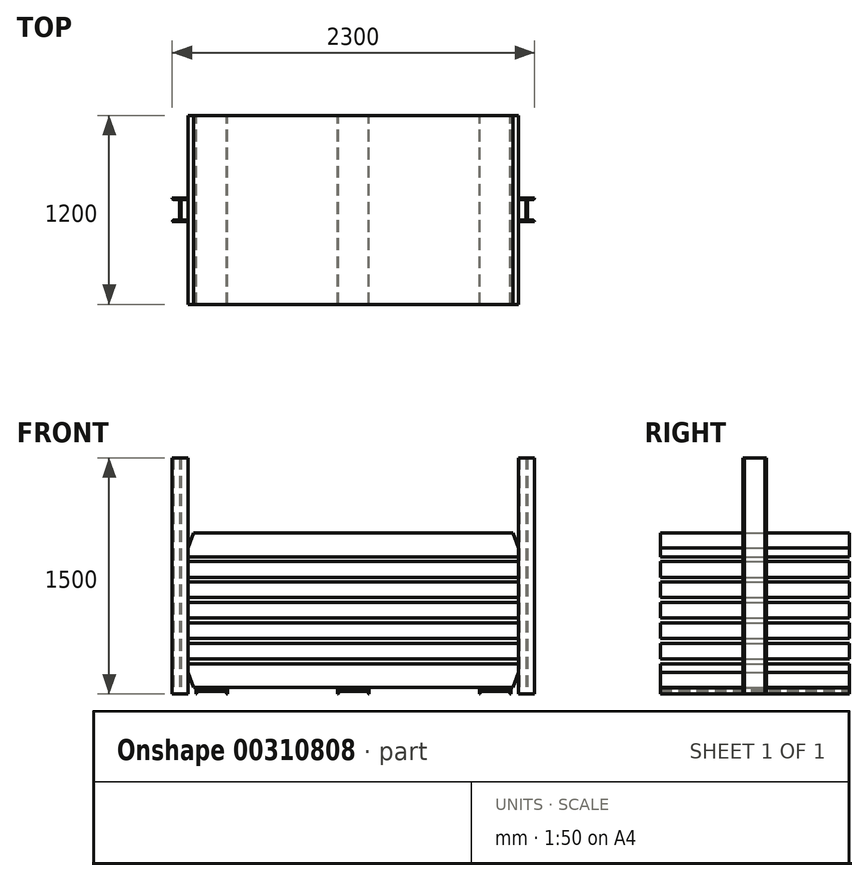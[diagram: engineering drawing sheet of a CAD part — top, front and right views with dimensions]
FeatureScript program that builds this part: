
annotation { "Feature Type Name" : "Feature", "Feature Type Description" : "" }
export const myFeature = defineFeature(function(context is Context, id is Id, definition is map)
    precondition{}
    {
        {
            var Q0;
            Q0=qCreatedBy(makeId("Front.planeOp"),FACE);
            var sketch = newSketch(context, id + "F0", { "sketchPlane" : qUnion([Q0])});
            skLineSegment(sketch, "E0", {"start": v(-100, 0) * mm, "end": v(100, 0) * mm, "construction": true});
            skLineSegment(sketch, "E1", {"start": v(0, -21.07) * mm, "end": v(0, 27.31) * mm, "construction": true});
            skPoint(sketch, "E1.startSnap0", {"position": v(0, 0) * mm});
            skLineSegment(sketch, "E2", {"start": v(-100, 20) * mm, "end": v(-100, -20) * mm});
            skLineSegment(sketch, "E3.0", {"start": v(-95, 15.24) * mm, "end": v(-95, 2.5) * mm});
            skLineSegment(sketch, "E4.0", {"start": v(-95, 2.5) * mm, "end": v(95, 2.5) * mm});
            skLineSegment(sketch, "E5.0", {"start": v(-95, -2.5) * mm, "end": v(95, -2.5) * mm});
            skLineSegment(sketch, "E6.trimOffspring", {"start": v(-95, -2.5) * mm, "end": v(-95, -15.24) * mm});
            skArc(sketch, "E7", {"start": v(-95, 15.24) * mm, "mid": v(-96.55, 18.62) * mm, "end": v(-100, 20) * mm});
            skArc(sketch, "E8.MirrorCS", {"start": v(-95, -15.24) * mm, "mid": v(-96.55, -18.62) * mm, "end": v(-100, -20) * mm});
            skLineSegment(sketch, "E9.MirrorCS", {"start": v(100, 20) * mm, "end": v(100, -20) * mm});
            skArc(sketch, "E10.MirrorCS", {"start": v(95, -15.24) * mm, "mid": v(96.55, -18.62) * mm, "end": v(100, -20) * mm});
            skLineSegment(sketch, "E11.MirrorCS", {"start": v(95, -2.5) * mm, "end": v(95, -15.24) * mm});
            skLineSegment(sketch, "E12.MirrorCS", {"start": v(95, 15.24) * mm, "end": v(95, 2.5) * mm});
            skArc(sketch, "E13.MirrorCS", {"start": v(95, 15.24) * mm, "mid": v(96.55, 18.62) * mm, "end": v(100, 20) * mm});
            skLineSegment(sketch, "E14.1.0.0", {"start": v(805, 2.5) * mm, "end": v(995, 2.5) * mm});
            skLineSegment(sketch, "E14.1.0.1", {"start": v(805, -2.5) * mm, "end": v(995, -2.5) * mm});
            skPoint(sketch, "E14.1.0.2", {"position": v(900, 0) * mm});
            skLineSegment(sketch, "E14.1.0.3", {"start": v(900, -21.07) * mm, "end": v(900, 27.31) * mm, "construction": true});
            skLineSegment(sketch, "E14.1.0.4", {"start": v(800, 0) * mm, "end": v(1000, 0) * mm, "construction": true});
            skLineSegment(sketch, "E14.1.0.5", {"start": v(1000, 20) * mm, "end": v(1000, -20) * mm});
            skArc(sketch, "E14.1.0.6", {"start": v(805, 15.24) * mm, "mid": v(803.45, 18.62) * mm, "end": v(800, 20) * mm});
            skLineSegment(sketch, "E14.1.0.7", {"start": v(995, -2.5) * mm, "end": v(995, -15.24) * mm});
            skLineSegment(sketch, "E14.1.0.8", {"start": v(800, 20) * mm, "end": v(800, -20) * mm});
            skLineSegment(sketch, "E14.1.0.9", {"start": v(995, 15.24) * mm, "end": v(995, 2.5) * mm});
            skLineSegment(sketch, "E14.1.0.10", {"start": v(805, 15.24) * mm, "end": v(805, 2.5) * mm});
            skLineSegment(sketch, "E14.1.0.11", {"start": v(805, -2.5) * mm, "end": v(805, -15.24) * mm});
            skArc(sketch, "E14.1.0.12", {"start": v(995, -15.24) * mm, "mid": v(996.55, -18.62) * mm, "end": v(1000, -20) * mm});
            skArc(sketch, "E14.1.0.13", {"start": v(805, -15.24) * mm, "mid": v(803.45, -18.62) * mm, "end": v(800, -20) * mm});
            skArc(sketch, "E14.1.0.14", {"start": v(995, 15.24) * mm, "mid": v(996.55, 18.62) * mm, "end": v(1000, 20) * mm});
            skLineSegment(sketch, "E14.direction1", {"start": v(-100, -20) * mm, "end": v(800, -20) * mm, "construction": true});
            skLineSegment(sketch, "E15.direction1", {"start": v(-100, -20) * mm, "end": v(-1000, -20) * mm, "construction": true});
            skPoint(sketch, "E16.orphan", {"position": v(-95, 15.24) * mm});
            skLineSegment(sketch, "E17.bottom", {"start": v(-1015, 22.23) * mm, "end": v(1015, 22.23) * mm});
            skLineSegment(sketch, "E17.top", {"start": v(-1050, 172.23) * mm, "end": v(1050, 172.23) * mm});
            skLineSegment(sketch, "E17.left", {"start": v(-1050, 117.23) * mm, "end": v(-1050, 172.23) * mm});
            skLineSegment(sketch, "E17.right", {"start": v(1050, 117.23) * mm, "end": v(1050, 172.23) * mm});
            skLineSegment(sketch, "E18", {"start": v(-1015, 22.23) * mm, "end": v(-1050, 117.23) * mm});
            skLineSegment(sketch, "E19.MirrorCS", {"start": v(1015, 22.23) * mm, "end": v(1050, 117.23) * mm});
            skLineSegment(sketch, "E20.bottom", {"start": v(-1050, 202.23) * mm, "end": v(1050, 202.23) * mm});
            skLineSegment(sketch, "E20.top", {"start": v(-1050, 302.23) * mm, "end": v(1050, 302.23) * mm});
            skLineSegment(sketch, "E20.left", {"start": v(-1050, 202.23) * mm, "end": v(-1050, 302.23) * mm});
            skLineSegment(sketch, "E20.right", {"start": v(1050, 202.23) * mm, "end": v(1050, 302.23) * mm});
            skLineSegment(sketch, "E21.0.1.0", {"start": v(-1050, 332.23) * mm, "end": v(1050, 332.23) * mm});
            skLineSegment(sketch, "E21.0.1.1", {"start": v(1050, 332.23) * mm, "end": v(1050, 432.23) * mm});
            skLineSegment(sketch, "E21.0.1.2", {"start": v(-1050, 332.23) * mm, "end": v(-1050, 432.23) * mm});
            skLineSegment(sketch, "E21.0.1.3", {"start": v(-1050, 432.23) * mm, "end": v(1050, 432.23) * mm});
            skLineSegment(sketch, "E21.0.2.0", {"start": v(-1050, 462.23) * mm, "end": v(1050, 462.23) * mm});
            skLineSegment(sketch, "E21.0.2.1", {"start": v(1050, 462.23) * mm, "end": v(1050, 562.23) * mm});
            skLineSegment(sketch, "E21.0.2.2", {"start": v(-1050, 462.23) * mm, "end": v(-1050, 562.23) * mm});
            skLineSegment(sketch, "E21.0.2.3", {"start": v(-1050, 562.23) * mm, "end": v(1050, 562.23) * mm});
            skLineSegment(sketch, "E21.0.3.0", {"start": v(-1050, 592.23) * mm, "end": v(1050, 592.23) * mm});
            skLineSegment(sketch, "E21.0.3.1", {"start": v(1050, 592.23) * mm, "end": v(1050, 692.23) * mm});
            skLineSegment(sketch, "E21.0.3.2", {"start": v(-1050, 592.23) * mm, "end": v(-1050, 692.23) * mm});
            skLineSegment(sketch, "E21.0.3.3", {"start": v(-1050, 692.23) * mm, "end": v(1050, 692.23) * mm});
            skLineSegment(sketch, "E21.direction1", {"start": v(-1050, 202.23) * mm, "end": v(-1025, 202.23) * mm, "construction": true});
            skLineSegment(sketch, "E21.direction2", {"start": v(-1050, 202.23) * mm, "end": v(-1050, 332.23) * mm, "construction": true});
            skLineSegment(sketch, "E22.0.1.0", {"start": v(-995, 2.5) * mm, "end": v(-805, 2.5) * mm});
            skLineSegment(sketch, "E22.3.1.0", {"start": v(-995, -2.5) * mm, "end": v(-805, -2.5) * mm});
            skPoint(sketch, "E22.6.1.0", {"position": v(-900, 0) * mm});
            skLineSegment(sketch, "E22.7.1.0", {"start": v(-1000, 0) * mm, "end": v(-800, 0) * mm, "construction": true});
            skLineSegment(sketch, "E22.10.1.0", {"start": v(-900, -21.07) * mm, "end": v(-900, 27.31) * mm, "construction": true});
            skArc(sketch, "E22.13.1.0", {"start": v(-805, -15.24) * mm, "mid": v(-803.45, -18.62) * mm, "end": v(-800, -20) * mm});
            skLineSegment(sketch, "E22.17.1.0", {"start": v(-805, -2.5) * mm, "end": v(-805, -15.24) * mm});
            skArc(sketch, "E22.20.1.0", {"start": v(-805, 15.24) * mm, "mid": v(-803.45, 18.62) * mm, "end": v(-800, 20) * mm});
            skLineSegment(sketch, "E22.24.1.0", {"start": v(-1000, 20) * mm, "end": v(-1000, -20) * mm});
            skLineSegment(sketch, "E22.27.1.0", {"start": v(-995, 15.24) * mm, "end": v(-995, 2.5) * mm});
            skPoint(sketch, "E22.28.1.0", {"position": v(-995, 15.24) * mm});
            skLineSegment(sketch, "E22.30.1.0", {"start": v(-995, -2.5) * mm, "end": v(-995, -15.24) * mm});
            skArc(sketch, "E22.33.1.0", {"start": v(-995, 15.24) * mm, "mid": v(-996.55, 18.62) * mm, "end": v(-1000, 20) * mm});
            skArc(sketch, "E22.37.1.0", {"start": v(-995, -15.24) * mm, "mid": v(-996.55, -18.62) * mm, "end": v(-1000, -20) * mm});
            skLineSegment(sketch, "E22.41.1.0", {"start": v(-800, 20) * mm, "end": v(-800, -20) * mm});
            skLineSegment(sketch, "E22.44.1.0", {"start": v(-805, 15.24) * mm, "end": v(-805, 2.5) * mm});
            skLineSegment(sketch, "E23.0.0.4", {"start": v(-1050, 722.23) * mm, "end": v(1050, 722.23) * mm});
            skLineSegment(sketch, "E23.3.0.4", {"start": v(1050, 722.23) * mm, "end": v(1050, 822.23) * mm});
            skLineSegment(sketch, "E23.6.0.4", {"start": v(-1050, 722.23) * mm, "end": v(-1050, 822.23) * mm});
            skLineSegment(sketch, "E23.9.0.4", {"start": v(-1050, 822.23) * mm, "end": v(1050, 822.23) * mm});
            skLineSegment(sketch, "E24", {"start": v(-1137.17, 512.23) * mm, "end": v(1108.9, 512.23) * mm, "construction": true});
            skPoint(sketch, "E24.startSnap0", {"position": v(-1050, 512.23) * mm});
            skPoint(sketch, "E24.endSnap0", {"position": v(1050, 512.23) * mm});
            skLineSegment(sketch, "E25.MirrorCS", {"start": v(-1050, 907.23) * mm, "end": v(-1050, 852.23) * mm});
            skLineSegment(sketch, "E26.MirrorCS", {"start": v(-1015, 1002.23) * mm, "end": v(-1050, 907.23) * mm});
            skLineSegment(sketch, "E27.MirrorCS", {"start": v(-1015, 1002.23) * mm, "end": v(1015, 1002.23) * mm});
            skLineSegment(sketch, "E28.MirrorCS", {"start": v(-1050, 852.23) * mm, "end": v(1050, 852.23) * mm});
            skLineSegment(sketch, "E29.MirrorCS", {"start": v(1015, 1002.23) * mm, "end": v(1050, 907.23) * mm});
            skLineSegment(sketch, "E30.MirrorCS", {"start": v(1050, 907.23) * mm, "end": v(1050, 852.23) * mm});
            skSolve(sketch);
        }
        {
            var Q0;
            Q0=makeQuery(id+"F0.imprint","IMPRINT",FACE,{"disambiguationData":[TD([[makeQuery(id+"F0.imprint","IMPRINT",EDGE,{"derivedFrom":sQuery(id+"F0.wireOp",EDGE,"E22.0.1.0")}),-1.0]])]});
            var Q1;
            Q1=makeQuery(id+"F0.imprint","IMPRINT",FACE,{"disambiguationData":[TD([[makeQuery(id+"F0.imprint","IMPRINT",EDGE,{"derivedFrom":sQuery(id+"F0.wireOp",EDGE,"E2")}),1.0]])]});
            var Q2;
            Q2=makeQuery(id+"F0.imprint","IMPRINT",FACE,{"disambiguationData":[TD([[makeQuery(id+"F0.imprint","IMPRINT",EDGE,{"derivedFrom":sQuery(id+"F0.wireOp",EDGE,"E14.1.0.0")}),-1.0]])]});
            extrude(context, id + "F1", {"entities" : qUnion([Q0, Q1, Q2]), "depth" : 1200 * mm, "symmetric" : true});
        }
        {
            var Q0;
            Q0=makeQuery(id+"F0.imprint","IMPRINT",FACE,{"disambiguationData":[TD([[makeQuery(id+"F0.imprint","IMPRINT",EDGE,{"derivedFrom":sQuery(id+"F0.wireOp",EDGE,"E17.bottom")}),1.0]])]});
            var Q1;
            Q1=makeQuery(id+"F0.imprint","IMPRINT",FACE,{"disambiguationData":[TD([[makeQuery(id+"F0.imprint","IMPRINT",EDGE,{"derivedFrom":sQuery(id+"F0.wireOp",EDGE,"E20.bottom")}),1.0]])]});
            var Q2;
            Q2=makeQuery(id+"F0.imprint","IMPRINT",FACE,{"disambiguationData":[TD([[makeQuery(id+"F0.imprint","IMPRINT",EDGE,{"derivedFrom":sQuery(id+"F0.wireOp",EDGE,"E21.0.1.0")}),1.0]])]});
            var Q3;
            Q3=makeQuery(id+"F0.imprint","IMPRINT",FACE,{"disambiguationData":[TD([[makeQuery(id+"F0.imprint","IMPRINT",EDGE,{"derivedFrom":sQuery(id+"F0.wireOp",EDGE,"E21.0.2.0")}),1.0]])]});
            var Q4;
            Q4=makeQuery(id+"F0.imprint","IMPRINT",FACE,{"disambiguationData":[TD([[makeQuery(id+"F0.imprint","IMPRINT",EDGE,{"derivedFrom":sQuery(id+"F0.wireOp",EDGE,"E21.0.3.0")}),1.0]])]});
            var Q5;
            Q5=makeQuery(id+"F0.imprint","IMPRINT",FACE,{"disambiguationData":[TD([[makeQuery(id+"F0.imprint","IMPRINT",EDGE,{"derivedFrom":sQuery(id+"F0.wireOp",EDGE,"E23.0.0.4")}),1.0]])]});
            var Q6;
            Q6=makeQuery(id+"F0.imprint","IMPRINT",FACE,{"disambiguationData":[TD([[makeQuery(id+"F0.imprint","IMPRINT",EDGE,{"derivedFrom":sQuery(id+"F0.wireOp",EDGE,"E25.MirrorCS")}),1.0]])]});
            extrude(context, id + "F2", {"entities" : qUnion([Q0, Q1, Q2, Q3, Q4, Q5, Q6]), "depth" : 1200 * mm, "symmetric" : true});
        }
        {
            var Q0;
            Q0=makeQuery(id+"F1.opExtrude","CAP_VERTEX",VERTEX,{"disambiguationData":[OSD([sQuery(id+"F0.wireOp",EDGE,"E14.1.0.5"),sQuery(id+"F0.wireOp",EDGE,"E14.1.0.12")])],"isStart":false});
            var Q1;
            Q1=makeQuery(id+"F1.opExtrude","CAP_VERTEX",VERTEX,{"disambiguationData":[OSD([sQuery(id+"F0.wireOp",EDGE,"E14.1.0.8"),sQuery(id+"F0.wireOp",EDGE,"E14.1.0.13")])],"isStart":false});
            var Q2;
            Q2=makeQuery(id+"F1.opExtrude","CAP_VERTEX",VERTEX,{"disambiguationData":[OSD([sQuery(id+"F0.wireOp",EDGE,"E14.1.0.8"),sQuery(id+"F0.wireOp",EDGE,"E14.1.0.13")])],"isStart":true});
            cPlane(context, id + "F3", {"entities" : qUnion([Q0, Q1, Q2]), "cplaneType" : CPlaneType.THREE_POINT, "offset" : 25 * mm, "width" : 150 * mm, "height" : 150 * mm});
        }
        {
            var Q0;
            Q0=qCreatedBy(id+"F3.planeOp",FACE);
            var sketch = newSketch(context, id + "F4", { "sketchPlane" : qUnion([Q0])});
            skPoint(sketch, "E31.0", {"position": v(1050, 0) * mm});
            skPoint(sketch, "E32.0", {"position": v(0, 0) * mm});
            skPoint(sketch, "E33.0", {"position": v(-1050, 0) * mm});
            skLineSegment(sketch, "E34", {"start": v(-1050, -113.08) * mm, "end": v(-1050, 136.34) * mm, "construction": true});
            skLineSegment(sketch, "E35", {"start": v(0, 136.34) * mm, "end": v(0, -148.25) * mm, "construction": true});
            skLineSegment(sketch, "E36", {"start": v(1050, -155.06) * mm, "end": v(1050, 136.34) * mm, "construction": true});
            skLineSegment(sketch, "E37", {"start": v(1272.36, 0) * mm, "end": v(-1293.89, 0) * mm, "construction": true});
            skLineSegment(sketch, "E38", {"start": v(1100, -75) * mm, "end": v(1100, 75) * mm, "construction": true});
            skLineSegment(sketch, "E39", {"start": v(1113.07, 0) * mm, "end": v(1050, 0) * mm, "construction": true});
            skPoint(sketch, "E39.startSnap0", {"position": v(1100, 0) * mm});
            skLineSegment(sketch, "E40", {"start": v(1050, -75) * mm, "end": v(1150, -75) * mm});
            skLineSegment(sketch, "E41.0", {"start": v(1056.88, -65) * mm, "end": v(1095, -65) * mm});
            skLineSegment(sketch, "E42.0", {"start": v(1095, -65) * mm, "end": v(1095, 65) * mm});
            skLineSegment(sketch, "E43.0", {"start": v(1105, -65) * mm, "end": v(1105, 65) * mm});
            skLineSegment(sketch, "E44.trimOffspring", {"start": v(1105, -65) * mm, "end": v(1143.12, -65) * mm});
            skArc(sketch, "E45", {"start": v(1056.88, -65) * mm, "mid": v(1051.88, -68.93) * mm, "end": v(1050, -75) * mm});
            skArc(sketch, "E46.MirrorCS", {"start": v(1143.12, -65) * mm, "mid": v(1148.12, -68.93) * mm, "end": v(1150, -75) * mm});
            skLineSegment(sketch, "E47.MirrorCS", {"start": v(1050, 75) * mm, "end": v(1150, 75) * mm});
            skArc(sketch, "E48.MirrorCS", {"start": v(1143.12, 65) * mm, "mid": v(1148.12, 68.93) * mm, "end": v(1150, 75) * mm});
            skLineSegment(sketch, "E49.MirrorCS", {"start": v(1105, 65) * mm, "end": v(1143.12, 65) * mm});
            skLineSegment(sketch, "E50.MirrorCS", {"start": v(1056.88, 65) * mm, "end": v(1095, 65) * mm});
            skArc(sketch, "E51.MirrorCS", {"start": v(1056.88, 65) * mm, "mid": v(1051.88, 68.93) * mm, "end": v(1050, 75) * mm});
            skPoint(sketch, "E52.orphan", {"position": v(1056.88, -65) * mm});
            skLineSegment(sketch, "E53", {"start": v(1050, -75) * mm, "end": v(1050, 75) * mm, "construction": true});
            skArc(sketch, "E54.MirrorCS", {"start": v(-1056.88, -65) * mm, "mid": v(-1051.88, -68.93) * mm, "end": v(-1050, -75) * mm});
            skArc(sketch, "E55.MirrorCS", {"start": v(-1143.12, -65) * mm, "mid": v(-1148.12, -68.93) * mm, "end": v(-1150, -75) * mm});
            skLineSegment(sketch, "E56.MirrorCS", {"start": v(-1095, -65) * mm, "end": v(-1095, 65) * mm});
            skLineSegment(sketch, "E57.MirrorCS", {"start": v(-1105, -65) * mm, "end": v(-1143.12, -65) * mm});
            skPoint(sketch, "E58.MirrorP", {"position": v(-1100, 0) * mm});
            skLineSegment(sketch, "E59.MirrorCS", {"start": v(-1105, -65) * mm, "end": v(-1105, 65) * mm});
            skLineSegment(sketch, "E60.MirrorCS", {"start": v(-1056.88, -65) * mm, "end": v(-1095, -65) * mm});
            skLineSegment(sketch, "E61.MirrorCS", {"start": v(-1100, -75) * mm, "end": v(-1100, 75) * mm, "construction": true});
            skLineSegment(sketch, "E62.MirrorCS", {"start": v(-1050, -75) * mm, "end": v(-1150, -75) * mm});
            skPoint(sketch, "E63.MirrorP", {"position": v(-1056.88, -65) * mm});
            skLineSegment(sketch, "E64.MirrorCS", {"start": v(-1050, 75) * mm, "end": v(-1150, 75) * mm});
            skArc(sketch, "E65.MirrorCS", {"start": v(-1143.12, 65) * mm, "mid": v(-1148.12, 68.93) * mm, "end": v(-1150, 75) * mm});
            skLineSegment(sketch, "E66.MirrorCS", {"start": v(-1105, 65) * mm, "end": v(-1143.12, 65) * mm});
            skLineSegment(sketch, "E67.MirrorCS", {"start": v(-1056.88, 65) * mm, "end": v(-1095, 65) * mm});
            skArc(sketch, "E68.MirrorCS", {"start": v(-1056.88, 65) * mm, "mid": v(-1051.88, 68.93) * mm, "end": v(-1050, 75) * mm});
            skSolve(sketch);
        }
        {
            var Q0;
            Q0 = qSketchRegion(id + "F4", true);
            extrude(context, id + "F5", {"entities" : qUnion([Q0]), "depth" : 1500 * mm});
        }
    });
